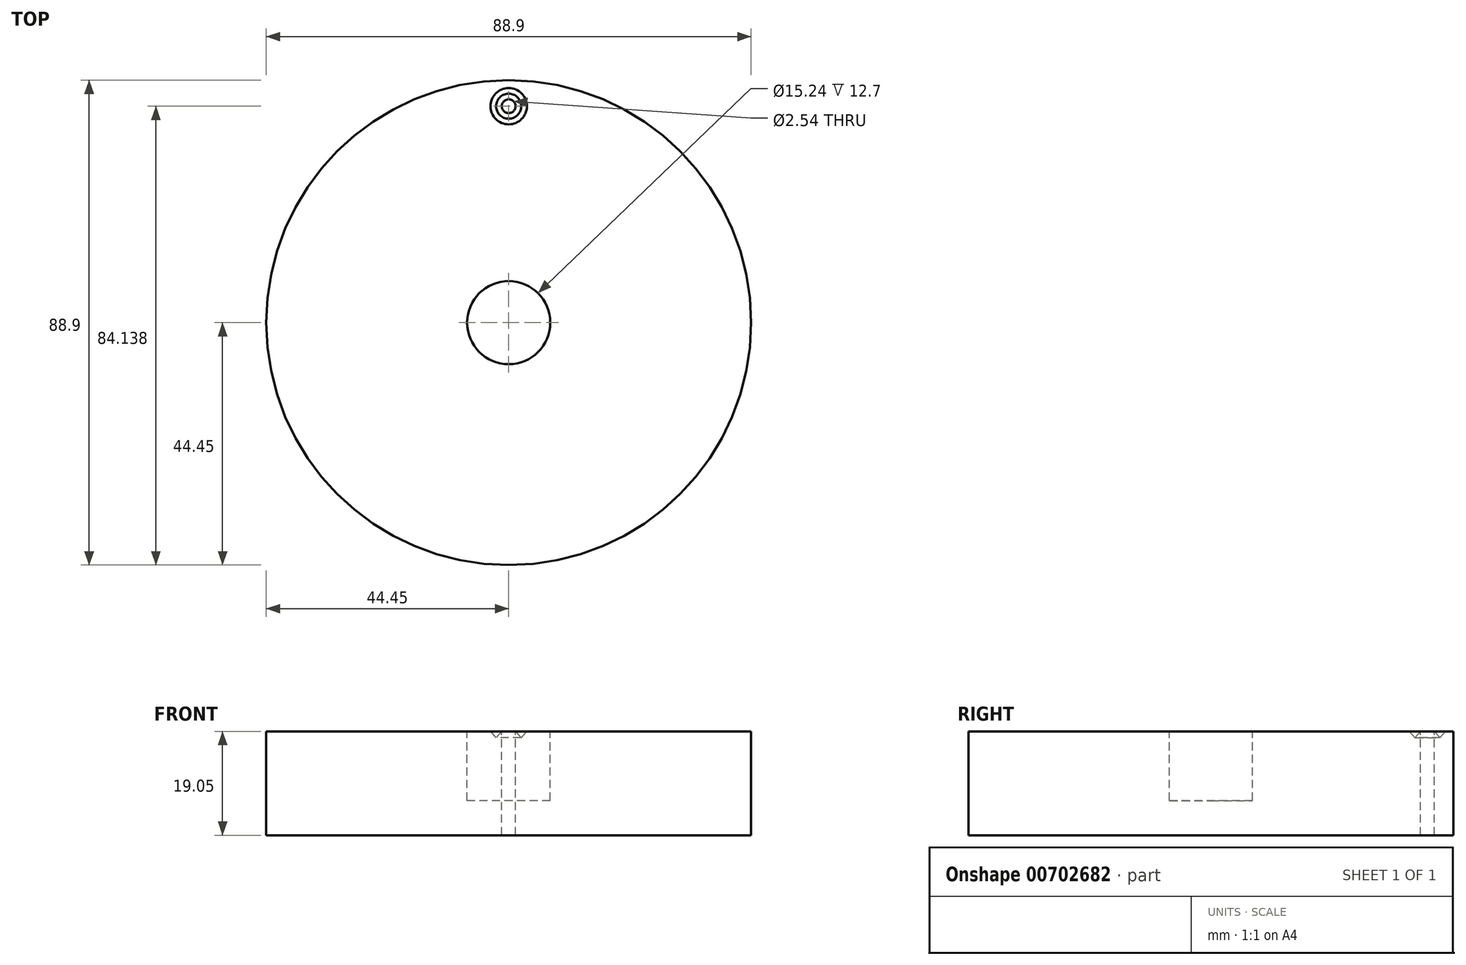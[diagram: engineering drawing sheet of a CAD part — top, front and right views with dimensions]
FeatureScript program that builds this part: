
annotation { "Feature Type Name" : "Feature", "Feature Type Description" : "" }
export const myFeature = defineFeature(function(context is Context, id is Id, definition is map)
    precondition{}
    {
        {
            var Q0;
            Q0=qCreatedBy(makeId("Top.planeOp"),FACE);
            var sketch = newSketch(context, id + "F0", { "sketchPlane" : qUnion([Q0])});
            skCircle(sketch, "E0", {"center": v(0, 0) * mm, "radius": 44.45 * mm});
            skSolve(sketch);
        }
        {
            var Q0;
            Q0 = qSketchRegion(id + "F0", true);
            extrude(context, id + "F1", {"entities" : qUnion([Q0]), "depth" : 19.05 * mm, "offsetDistance" : 25.4 * mm});
        }
        {
            var Q0;
            Q0=makeQuery(id+"F1.opExtrude","CAP_FACE",FACE,{"disambiguationData":[OSD([sQuery(id+"F0.wireOp",EDGE,"E0")])],"isStart":false});
            var sketch = newSketch(context, id + "F2", { "sketchPlane" : qUnion([Q0])});
            skCircle(sketch, "E1", {"center": v(0, 0) * mm, "radius": 7.62 * mm});
            skSolve(sketch);
        }
        {
            var Q0;
            Q0 = qSketchRegion(id + "F2", true);
            extrude(context, id + "F3", {"entities" : qUnion([Q0]), "operationType" : NewBodyOperationType.REMOVE, "oppositeDirection" : true, "depth" : 12.7 * mm, "offsetDistance" : 25.4 * mm});
        }
        {
            var Q0;
            Q0=makeQuery(id+"F1.opExtrude","CAP_FACE",FACE,{"disambiguationData":[OSD([sQuery(id+"F0.wireOp",EDGE,"E0")])],"isStart":false});
            var sketch = newSketch(context, id + "F4", { "sketchPlane" : qUnion([Q0])});
            skCircle(sketch, "E2", {"center": v(0, 39.69) * mm, "radius": 1.27 * mm});
            skSolve(sketch);
        }
        {
            var Q0;
            Q0=makeQuery(id+"F4.imprint","IMPRINT",FACE,{"disambiguationData":[TD([[makeQuery(id+"F4.imprint","IMPRINT",EDGE,{"derivedFrom":sQuery(id+"F4.wireOp",EDGE,"E2")}),1.0]])]});
            extrude(context, id + "F5", {"entities" : qUnion([Q0]), "operationType" : NewBodyOperationType.REMOVE, "endBound" : BoundingType.THROUGH_ALL, "oppositeDirection" : true, "depth" : 25.4 * mm, "offsetDistance" : 25.4 * mm});
        }
        {
            var Q0;
            Q0=makeQuery(id+"F1.opExtrude","CAP_FACE",FACE,{"disambiguationData":[OSD([sQuery(id+"F0.wireOp",EDGE,"E0")])],"isStart":false});
            var sketch = newSketch(context, id + "F6", { "sketchPlane" : qUnion([Q0])});
            skCircle(sketch, "E3", {"center": v(0, 39.69) * mm, "radius": 3.33 * mm});
            skSolve(sketch);
        }
        {
            var Q0;
            Q0=makeQuery(id+"F6.imprint","IMPRINT",FACE,{"disambiguationData":[TD([[makeQuery(id+"F6.imprint","IMPRINT",EDGE,{"derivedFrom":sQuery(id+"F6.wireOp",EDGE,"E3")}),1.0]])]});
            extrude(context, id + "F7", {"entities" : qUnion([Q0]), "operationType" : NewBodyOperationType.REMOVE, "oppositeDirection" : true, "depth" : 2.1 * mm, "offsetDistance" : 25.4 * mm, "hasDraft" : true, "draftAngle" : 41 * degree, "draftPullDirection" : true});
        }
    });
